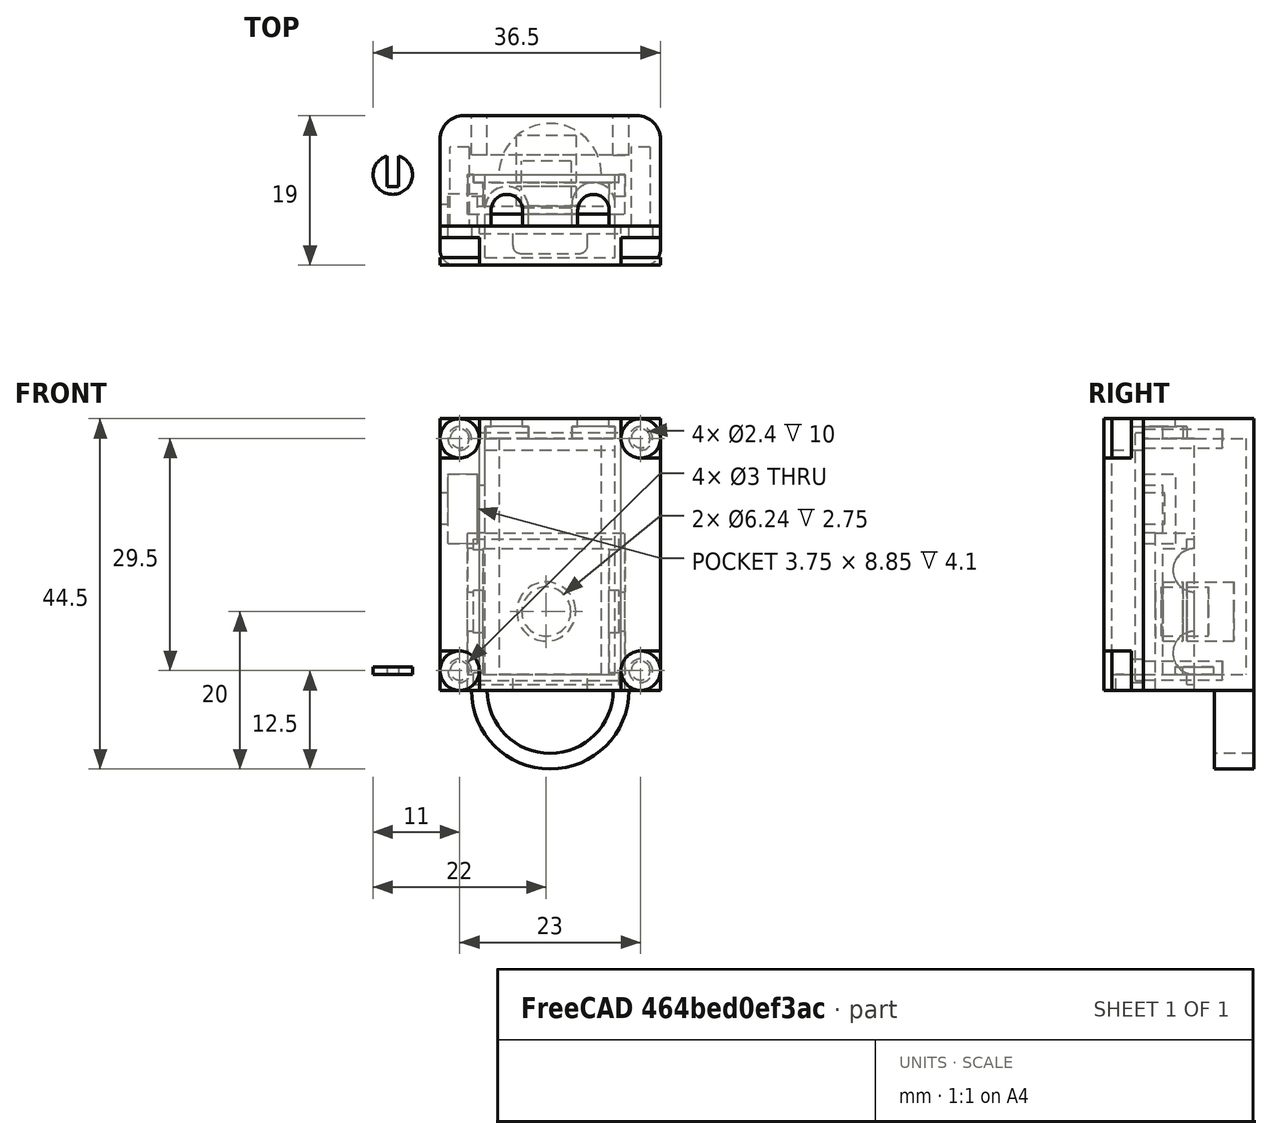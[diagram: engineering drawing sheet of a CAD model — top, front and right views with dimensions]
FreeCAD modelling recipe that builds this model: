
FCSTD DOCUMENT  (FreeCAD 0.20R29410 (Git))
Label: light_up_lanyard
License: All rights reserved
LicenseURL: http://en.wikipedia.org/wiki/All_rights_reserved
objects: Part::Cylinder×28, Part::Box×21, Part::Cut×7, Part::Fillet×7, Part::MultiFuse×5
note: 68 computed .brp shape members not serialized (recipe doc carries the construction recipe); baked Part::Feature solids carry a one-line shape summary decoded from their .brp

FEATURE [Part::Box] Box  label="Cube(outer_female)"
  AttacherType = Attacher::AttachEngine3D
  Height = 34.5
  Length = 28
  Placement = pos=(-14,-6.5,-2) rot=(0,0,1;0rad)
  Width = 14
FEATURE [Part::Box] Box002  label="Cube002(inner_female_lip)"
  AttacherType = Attacher::AttachEngine3D
  Height = 31.5
  Length = 18
  Placement = pos=(-9,-7.5,-0.75) rot=(0,0,1;0rad)
  Width = 1
FEATURE [Part::Box] Box004  label="Cube(outer_male)"
  AttacherType = Attacher::AttachEngine3D
  Height = 20
  Length = 20
  Placement = pos=(-10.5,-5,-2) rot=(0,0,1;0rad)
  Width = 5
FEATURE [Part::Box] Box005  label="Cube002(inner_male)"
  AttacherType = Attacher::AttachEngine3D
  Height = 16
  Length = 16
  Placement = pos=(-8.5,-4,0) rot=(0,0,1;0rad)
  Width = 4
FEATURE [Part::Box] Box017  label="Cube(inner_female)"
  AttacherType = Attacher::AttachEngine3D
  Height = 30
  Length = 16.5
  Placement = pos=(-8.25,-6.5,0) rot=(0,0,1;0rad)
  Width = 6.5
FEATURE [Part::Cylinder] Cylinder002  label="Cylinder002(lanyard_outer_female)"
  Angle = 180
  AttacherType = Attacher::AttachEngine3D
  FirstAngle = 0
  Height = 5
  Placement = pos=(0,2.5,-2) rot=(-1,0,0;1.5708rad)
  Radius = 10
  SecondAngle = 0
FEATURE [Part::Cylinder] Cylinder003  label="Cylinder003(lanyard_inner_female)"
  Angle = 180
  AttacherType = Attacher::AttachEngine3D
  FirstAngle = 0
  Height = 5
  Placement = pos=(0,2.5,-2) rot=(-1,0,0;1.5708rad)
  Radius = 8
  SecondAngle = 0
FEATURE [Part::Cut] Cut
  Base = -> Cylinder002
  Tool = -> Cylinder003
FEATURE [Part::Cylinder] Cylinder015  label="Cylinder(magnet_inner)"
  Angle = 360
  AttacherType = Attacher::AttachEngine3D
  FirstAngle = 0
  Height = 2.75
  Placement = pos=(-0.5,-1.5,8) rot=(1,0,0;1.5708rad)
  Radius = 3.12
  SecondAngle = 0
FEATURE [Part::Cylinder] Cylinder016  label="Cylinder(magnet_outer)"
  Angle = 360
  AttacherType = Attacher::AttachEngine3D
  FirstAngle = 0
  Height = 3.5
  Placement = pos=(-0.5,-1.5,8) rot=(1,0,0;1.5708rad)
  Radius = 3.75
  SecondAngle = 0
FEATURE [Part::Cylinder] Cylinder017  label="Cylinder(magnet_inner)001"
  Angle = 360
  AttacherType = Attacher::AttachEngine3D
  FirstAngle = 0
  Height = 2.75
  Placement = pos=(-0.5,1.75,8) rot=(1,0,0;1.5708rad)
  Radius = 3.12
  SecondAngle = 0
FEATURE [Part::Cylinder] Cylinder018  label="Cylinder(magnet_outer)001"
  Angle = 360
  AttacherType = Attacher::AttachEngine3D
  FirstAngle = 0
  Height = 6
  Placement = pos=(-0.5,5,8) rot=(1,0,0;1.5708rad)
  Radius = 3.75
  SecondAngle = 0
FEATURE [Part::Cut] Cut069  label="Cut069(magnet_holder_bottom)"
  Base = -> Cylinder018
  Tool = -> Cylinder017
FEATURE [Part::Cylinder] Cylinder019  label="Cylinder001(para_hole_right_female_top)"
  Angle = 360
  AttacherType = Attacher::AttachEngine3D
  FirstAngle = 0
  Height = 2
  Placement = pos=(7.5,0,13.25) rot=(0,1,0;1.5708rad)
  Radius = 2.75
  SecondAngle = 0
FEATURE [Part::Cylinder] Cylinder020  label="Cylinder(para_hole_right_female_bottom)"
  Angle = 360
  AttacherType = Attacher::AttachEngine3D
  FirstAngle = 0
  Height = 2
  Placement = pos=(7.5,0,2.75) rot=(0,1,0;1.5708rad)
  Radius = 2.75
  SecondAngle = 0
FEATURE [Part::Box] Box020  label="Cube002(inner_male_lip)"
  AttacherType = Attacher::AttachEngine3D
  Height = 18.5
  Length = 18.5
  Placement = pos=(-9.75,-1,-1.25) rot=(0,0,1;0rad)
  Width = 1
FEATURE [Part::Cylinder] Cylinder023  label="Cylinder001(para_hole_left_female_top)001"
  Angle = 360
  AttacherType = Attacher::AttachEngine3D
  FirstAngle = 0
  Height = 2
  Placement = pos=(-10.5,0,13.25) rot=(0,1,0;1.5708rad)
  Radius = 2.75
  SecondAngle = 0
FEATURE [Part::Cylinder] Cylinder024  label="Cylinder(para_hole_left_female_bottom)001"
  Angle = 360
  AttacherType = Attacher::AttachEngine3D
  FirstAngle = 0
  Height = 2
  Placement = pos=(-10.5,0,2.75) rot=(0,1,0;1.5708rad)
  Radius = 2.75
  SecondAngle = 0
FEATURE [Part::MultiFuse] Fusion
  Shapes = -> [Box005,Cylinder019,Cylinder020,Box020,Cylinder023,Cylinder024]
FEATURE [Part::Cut] Cut073
  Base = -> Box004
  Tool = -> Fusion
FEATURE [Part::MultiFuse] Fusion008
  Shapes = -> [Cut073,Cylinder016]
FEATURE [Part::Cut] Cut074
  Base = -> Fusion008
  Tool = -> Cylinder015
FEATURE [Part::Cylinder] Cylinder025  label="Cylinder(battery)"
  Angle = 360
  AttacherType = Attacher::AttachEngine3D
  FirstAngle = 0
  Height = 30
  Radius = 6.5
  SecondAngle = 0
FEATURE [Part::Box] Box023  label="Cube(pcb)"
  AttacherType = Attacher::AttachEngine3D
  Height = 28.5
  Length = 16.5
  Placement = pos=(-8.25,-10.5,0) rot=(0,0,1;0rad)
  Width = 4
FEATURE [Part::Box] Box024  label="Cube(switch_body)"
  AttacherType = Attacher::AttachEngine3D
  Height = 8.85
  Length = 3.75
  Placement = pos=(-13,-6.5,21.15) rot=(0,0,1;0rad)
  Width = 4.1
FEATURE [Part::Box] Box025  label="Cube(switch_pins)"
  AttacherType = Attacher::AttachEngine3D
  Height = 6
  Length = 1
  Placement = pos=(-9.25,-6.5,22.57) rot=(0,0,1;0rad)
  Width = 2.5
FEATURE [Part::Box] Box026  label="Cube(switch_switch)"
  AttacherType = Attacher::AttachEngine3D
  Height = 4
  Length = 1
  Placement = pos=(-14,-6.5,23.62) rot=(0,0,1;0rad)
  Width = 2.75
FEATURE [Part::MultiFuse] Fusion009
  Placement = pos=(0,0,-4.5) rot=(0,0,1;0rad)
  Shapes = -> [Box026,Box024,Box025]
FEATURE [Part::Cylinder] Cylinder  label="Cylinder(thread_top_left)"
  Angle = 360
  AttacherType = Attacher::AttachEngine3D
  FirstAngle = 0
  Height = 10
  Placement = pos=(-11.5,3.5,30) rot=(1,0,0;1.5708rad)
  Radius = 1.2
  SecondAngle = 0
FEATURE [Part::Cylinder] Cylinder026  label="Cylinder(bolt_head_top_left)"
  Angle = 360
  AttacherType = Attacher::AttachEngine3D
  FirstAngle = 0
  Height = 1
  Placement = pos=(-11.5,-10.5,30) rot=(1,0,0;1.5708rad)
  Radius = 2.5
  SecondAngle = 0
FEATURE [Part::Cylinder] Cylinder027  label="Cylinder(thread_bottom)right)"
  Angle = 360
  AttacherType = Attacher::AttachEngine3D
  FirstAngle = 0
  Height = 10
  Placement = pos=(11.5,3.5,0.5) rot=(1,0,0;1.5708rad)
  Radius = 1.2
  SecondAngle = 0
FEATURE [Part::Cylinder] Cylinder028  label="Cylinder(bolt_head_bottom_right)"
  Angle = 360
  AttacherType = Attacher::AttachEngine3D
  FirstAngle = 0
  Height = 1
  Placement = pos=(11.5,-10.5,0.5) rot=(1,0,0;1.5708rad)
  Radius = 2.5
  SecondAngle = 0
FEATURE [Part::Cylinder] Cylinder029  label="Cylinder(paracord_left)"
  Angle = 360
  AttacherType = Attacher::AttachEngine3D
  FirstAngle = 0
  Height = 1
  Placement = pos=(-5.5,-4.5,31.5) rot=(0,0,1;0rad)
  Radius = 2
  SecondAngle = 0
FEATURE [Part::Cylinder] Cylinder030  label="Cylinder(paracord_right)"
  Angle = 360
  AttacherType = Attacher::AttachEngine3D
  FirstAngle = 0
  Height = 1
  Placement = pos=(5.5,-4.5,31.5) rot=(0,0,1;0rad)
  Radius = 2
  SecondAngle = 0
FEATURE [Part::Cylinder] Cylinder031  label="Cylinder(paracord_stopper_left)"
  Angle = 360
  AttacherType = Attacher::AttachEngine3D
  FirstAngle = 0
  Height = 1.5
  Placement = pos=(-5.5,-4.25,30) rot=(0,0,1;0rad)
  Radius = 2.75
  SecondAngle = 0
FEATURE [Part::Box] Box027  label="Cube(paracord_stopper_top_left)"
  AttacherType = Attacher::AttachEngine3D
  Height = 1.5
  Length = 5.5
  Placement = pos=(-8.25,-6.5,30) rot=(0,0,1;0rad)
  Width = 2.5
FEATURE [Part::Cylinder] Cylinder032  label="Cylinder(paracord_stopper_right)"
  Angle = 360
  AttacherType = Attacher::AttachEngine3D
  FirstAngle = 0
  Height = 1.5
  Placement = pos=(5.5,-3.75,30) rot=(0,0,1;0rad)
  Radius = 2.75
  SecondAngle = 0
FEATURE [Part::Box] Box028  label="Cube(paracord_stopper_top_right)"
  AttacherType = Attacher::AttachEngine3D
  Height = 1.5
  Length = 5.5
  Placement = pos=(2.75,-6.5,30) rot=(0,0,1;0rad)
  Width = 2.5
FEATURE [Part::Box] Box029  label="Cube(paracord_cutter_left)"
  AttacherType = Attacher::AttachEngine3D
  Height = 1
  Length = 4
  Placement = pos=(-7.5,-6.5,31.5) rot=(0,0,1;0rad)
  Width = 2
FEATURE [Part::Box] Box030  label="Cube(paracord_cutter_right)"
  AttacherType = Attacher::AttachEngine3D
  Height = 1
  Length = 4
  Placement = pos=(3.5,-6.5,31.5) rot=(0,0,1;0rad)
  Width = 2
FEATURE [Part::Fillet] Fillet
  Base = -> Box
  Edges = 2 edges r=3: [Edge3,Edge7]
FEATURE [Part::Cylinder] Cylinder033  label="Cylinder"
  Angle = 360
  AttacherType = Attacher::AttachEngine3D
  FirstAngle = 0
  Height = 1
  Placement = pos=(-20,0,0) rot=(0,0,1;0rad)
  Radius = 2.5
  SecondAngle = 0
FEATURE [Part::Box] Box031  label="Cube"
  AttacherType = Attacher::AttachEngine3D
  Height = 1
  Length = 1.5
  Placement = pos=(-20.75,-1.5,0) rot=(0,0,1;0rad)
  Width = 4
FEATURE [Part::Cut] Cut076
  Base = -> Cylinder033
  Tool = -> Box031
FEATURE [Part::Box] Box032  label="Cube001(usb_c_port)"
  AttacherType = Attacher::AttachEngine3D
  Height = 2
  Length = 9.5
  Placement = pos=(-4.75,-10,-2) rot=(0,0,1;0rad)
  Width = 3.5
FEATURE [Part::Box] Box033  label="Cube(lid)"
  AttacherType = Attacher::AttachEngine3D
  Height = 34.5
  Length = 28
  Placement = pos=(-14,-11.5,-2) rot=(0,0,1;0rad)
  Width = 5
FEATURE [Part::Cylinder] Cylinder034  label="Cylinder(bolt_clear_top_left)"
  Angle = 360
  AttacherType = Attacher::AttachEngine3D
  FirstAngle = 0
  Height = 1.5
  Placement = pos=(-11.5,-6.5,30) rot=(1,0,0;1.5708rad)
  Radius = 1.5
  SecondAngle = 0
FEATURE [Part::Cylinder] Cylinder035  label="Cylinder(bolt_clear_bottom_right)"
  Angle = 360
  AttacherType = Attacher::AttachEngine3D
  FirstAngle = 0
  Height = 1.5
  Placement = pos=(11.5,-6.5,0.5) rot=(1,0,0;1.5708rad)
  Radius = 1.5
  SecondAngle = 0
FEATURE [Part::Fillet] Fillet001
  Base = -> Box033
  Edges = 2 edges r=2: [Edge1,Edge5]
FEATURE [Part::Fillet] Fillet002
  Base = -> Box032
  Edges = 2 edges r=1: [Edge1,Edge5]
FEATURE [Part::Box] Box034  label="Cube001(bolt_head_bottom_right)"
  AttacherType = Attacher::AttachEngine3D
  Height = 5
  Length = 5
  Placement = pos=(9,-12,-2) rot=(0,0,1;0rad)
  Width = 4
FEATURE [Part::Box] Box035  label="Cube001(bolt_head_top_left)"
  AttacherType = Attacher::AttachEngine3D
  Height = 5
  Length = 5
  Placement = pos=(-14,-12,27.5) rot=(0,0,1;0rad)
  Width = 4
FEATURE [Part::Cylinder] Cylinder036  label="Cylinder(bolt_head_bottom_left)"
  Angle = 360
  AttacherType = Attacher::AttachEngine3D
  FirstAngle = 0
  Height = 1
  Placement = pos=(-11.5,-10.5,0.5) rot=(1,0,0;1.5708rad)
  Radius = 2.5
  SecondAngle = 0
FEATURE [Part::Cylinder] Cylinder037  label="Cylinder(bolt_head_top_right)"
  Angle = 360
  AttacherType = Attacher::AttachEngine3D
  FirstAngle = 0
  Height = 1
  Placement = pos=(11.5,-10.5,30) rot=(1,0,0;1.5708rad)
  Radius = 2.5
  SecondAngle = 0
FEATURE [Part::Cylinder] Cylinder038  label="Cylinder(thread_top_right)"
  Angle = 360
  AttacherType = Attacher::AttachEngine3D
  FirstAngle = 0
  Height = 10
  Placement = pos=(11.5,3.5,30) rot=(1,0,0;1.5708rad)
  Radius = 1.2
  SecondAngle = 0
FEATURE [Part::Cylinder] Cylinder039  label="Cylinder(thread_bottom_left)"
  Angle = 360
  AttacherType = Attacher::AttachEngine3D
  FirstAngle = 0
  Height = 10
  Placement = pos=(-11.5,3.5,0.5) rot=(1,0,0;1.5708rad)
  Radius = 1.2
  SecondAngle = 0
FEATURE [Part::MultiFuse] Fusion012
  Shapes = -> [Cylinder039,Cylinder038,Box030,Box029,Box028,Cylinder032,Box027,Cylinder031,Cylinder030,Cylinder029,Cylinder027,Cylinder,Fusion009,Cylinder025,Box017]
FEATURE [Part::Cut] Cut077
  Base = -> Fillet
  Tool = -> Fusion012
FEATURE [Part::Box] Box036  label="Cube001(bolt_head_top_right)"
  AttacherType = Attacher::AttachEngine3D
  Height = 5
  Length = 5
  Placement = pos=(9,-12,27.5) rot=(0,0,1;0rad)
  Width = 4
FEATURE [Part::Box] Box037  label="Cube001(bolt_head_bottom_left)"
  AttacherType = Attacher::AttachEngine3D
  Height = 5
  Length = 5
  Placement = pos=(-14,-12,-2) rot=(0,0,1;0rad)
  Width = 4
FEATURE [Part::Cylinder] Cylinder040  label="Cylinder(bolt_clear_bottom_left)"
  Angle = 360
  AttacherType = Attacher::AttachEngine3D
  FirstAngle = 0
  Height = 1.5
  Placement = pos=(-11.5,-6.5,0.5) rot=(1,0,0;1.5708rad)
  Radius = 1.5
  SecondAngle = 0
FEATURE [Part::Cylinder] Cylinder041  label="Cylinder(bolt_clear_top_right)"
  Angle = 360
  AttacherType = Attacher::AttachEngine3D
  FirstAngle = 0
  Height = 1.5
  Placement = pos=(11.5,-6.5,30) rot=(1,0,0;1.5708rad)
  Radius = 1.5
  SecondAngle = 0
FEATURE [Part::Fillet] Fillet003
  Base = -> Box035
  Edges = 1 edges r=2.5: [Edge8]
FEATURE [Part::Fillet] Fillet004
  Base = -> Box036
  Edges = 1 edges r=2.5: [Edge4]
FEATURE [Part::Fillet] Fillet005
  Base = -> Box037
  Edges = 1 edges r=2.5: [Edge6]
FEATURE [Part::Fillet] Fillet006
  Base = -> Box034
  Edges = 1 edges r=2.5: [Edge2]
FEATURE [Part::MultiFuse] Fusion013
  Shapes = -> [Fillet005,Fillet006,Fillet004,Fillet003,Cylinder041,Cylinder040,Fillet002,Cylinder035,Cylinder034,Box023]
FEATURE [Part::Cut] Cut078  label="Cut078(lid)"
  Base = -> Fillet001
  Tool = -> Fusion013
